# Revit family: Reece_Toilet_Roca_The Gap_Back to Wall
name_source: partatom
category: Plumbing Fixtures
revit_build: Autodesk Revit 2018 (Build: 20180329_1100(x64)
units: mm (PartAtom-declared; Revit-internal decimal feet)

## family parameters
Always vertical = Yes
Cut with Voids When Loaded = No
Part Type = Normal
Room Calculation Point = No
Round Connector Dimension = Use Diameter
Shared = No
Work Plane-Based = No

## types (1)
- Vitreous China_White
    Description = The Gap Back To Wall Comfort Height Pan with Seat White (4 Star)

The Gap Back To Wall Comfort Height Pan with Seat White (4 Star)
The Gap Back To Wall Comfort Height Pan with Seat White (4 Star)
The Gap Back To Wall Comfort Height Pan with Seat White (4 Star)
    Disclaimer = THIS FILE IS THE PROPERTY OF THE REECE GROUP. IT MAY NOT BE REPRODUCED, REVERSE-ENGINEERED OR MODIFIED. ANY REPUBLICATION, TRANSMISSION OR DISTRIBUTION FOR THE PURPOSE OF COMMERCIALLY EXPLOITING THE FILES IS PROHIBITED.
    Keynote = Product #9505425, Reece_Toilet_Roca_The Gap_Back to Wall - Vitreous China_White
    Manufacturer = Roca
    Model = The Gap
    Reece_Back_Inlet = 55 mm  [stored 0.180446 ft]
    Reece_Back_Outlet_Offset = 180 mm  [stored 0.590551 ft]
    Reece_Bottom_Outlet_Offset = 95 mm
    Reece_Detail_Additional = Pan Back to Wall
    Reece_Detail_Connector = Back Inlet
    Reece_Detail_Disclaimer = THIS FILE IS THE PROPERTY OF THE REECE GROUP. IT MAY NOT BE REPRODUCED, REVERSE-ENGINEERED OR MODIFIED. ANY REPUBLICATION, TRANSMISSION OR DISTRIBUTION FOR THE PURPOSE OF COMMERCIALLY EXPLOITING THE FILES IS PROHIBITED.
    Reece_Detail_Installation = Universal S & P
    Reece_Material-Cistern = Reece_Vitreous China_White
    Reece_Material_Main = Reece_Vitreous China_White
    Reece_Material_Seat = Reece_Acrylic_White
    Reece_Overall_Height = 480 mm
    Reece_Overall_Projection = 610 mm  [stored 2.00131 ft]
    Reece_Overall_Width = 350 mm  [stored 1.14829 ft]
    Reece_P_Trap = 102 mm
    Reece_Pan_Height = 440 mm  [stored 1.44357 ft]
    Reece_Product_Brand = Roca
    Reece_Product_Description = Roca The Gap Back To Wall Comfort Height Pan with Seat White (4 Star)
    Reece_Product_Mount = Floor Mounted
    Reece_Product_Number = 9505425
    Reece_Product_Sub Brand = The Gap
    Reece_Product_Web Page = https://www.reece.com.au
    Reece_S_Trap = 102 mm
    URL = https://www.reece.com.au

note: [stored X ft] marks values corroborated as IEEE doubles in the binary element streams (Revit-internal decimal feet)

## geometry (parser evidence)
native form markers: Sweep x8
no freeform markers — native parametric forms only
